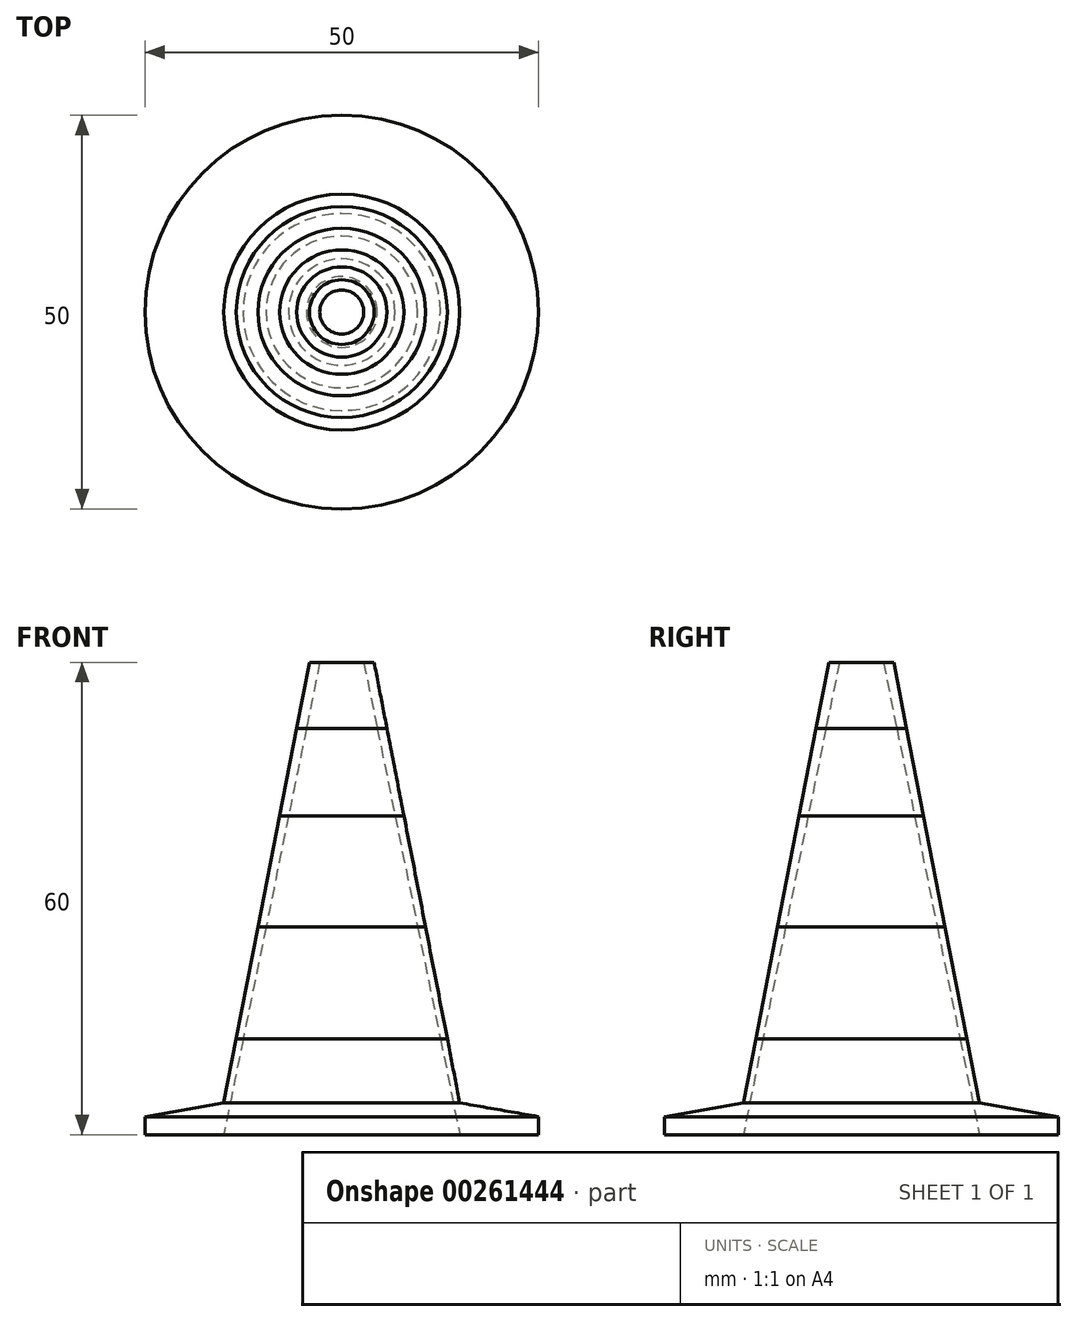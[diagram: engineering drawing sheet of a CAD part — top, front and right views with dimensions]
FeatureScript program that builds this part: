
annotation { "Feature Type Name" : "Feature", "Feature Type Description" : "" }
export const myFeature = defineFeature(function(context is Context, id is Id, definition is map)
    precondition{}
    {
        {
            var Q0;
            Q0=qCreatedBy(makeId("Front.planeOp"),FACE);
            var sketch = newSketch(context, id + "F0", { "sketchPlane" : qUnion([Q0])});
            skLineSegment(sketch, "E0", {"start": v(-25, 0) * mm, "end": v(-25, 2.28) * mm});
            skLineSegment(sketch, "E1", {"start": v(-25, 2.28) * mm, "end": v(-14.98, 4.05) * mm});
            skLineSegment(sketch, "E2", {"start": v(-14.98, 4.05) * mm, "end": v(-4.1, 60) * mm});
            skLineSegment(sketch, "E3", {"start": v(-4.1, 60) * mm, "end": v(0, 60) * mm});
            skLineSegment(sketch, "E4", {"start": v(0, 60) * mm, "end": v(0, 0) * mm});
            skLineSegment(sketch, "E5", {"start": v(0, 0) * mm, "end": v(-25, 0) * mm});
            skLineSegment(sketch, "E6", {"start": v(-13.4, 12.2) * mm, "end": v(0, 12.2) * mm});
            skLineSegment(sketch, "E7", {"start": v(-10.64, 26.4) * mm, "end": v(0, 26.4) * mm});
            skLineSegment(sketch, "E8", {"start": v(-5.74, 51.6) * mm, "end": v(0, 51.6) * mm});
            skLineSegment(sketch, "E9", {"start": v(-7.9, 40.5) * mm, "end": v(0, 40.5) * mm});
            skSolve(sketch);
        }
        {
            var Q0;
            {var subQ0=sQuery(id+"F0.wireOp",EDGE,"E3");Q0=makeQuery(id+"F0.imprint","IMPRINT",FACE,{"disambiguationData":[TD([[makeQuery(id+"F0.imprint","IMPRINT",EDGE,{"derivedFrom":subQ0}),-1.0]])]});}
            var Q1;
            Q1=sQuery(id+"F0.wireOp",EDGE,"E4");
            revolve(context, id + "F1", {"entities" : qUnion([Q0]), "axis" : qUnion([Q1]), "revolveType" : RevolveType.FULL});
        }
        {
            var Q0;
            {var subQ0=sQuery(id+"F0.wireOp",EDGE,"E8");Q0=makeQuery(id+"F0.imprint","IMPRINT",FACE,{"disambiguationData":[TD([[makeQuery(id+"F0.imprint","IMPRINT",EDGE,{"derivedFrom":subQ0}),-1.0]])]});}
            var Q1;
            Q1=sQuery(id+"F0.wireOp",EDGE,"E4");
            revolve(context, id + "F2", {"entities" : qUnion([Q0]), "axis" : qUnion([Q1]), "revolveType" : RevolveType.FULL});
        }
        {
            var Q0;
            {var subQ0=sQuery(id+"F0.wireOp",EDGE,"E7");Q0=makeQuery(id+"F0.imprint","IMPRINT",FACE,{"disambiguationData":[TD([[makeQuery(id+"F0.imprint","IMPRINT",EDGE,{"derivedFrom":subQ0}),1.0]])]});}
            var Q1;
            Q1=sQuery(id+"F0.wireOp",EDGE,"E4");
            revolve(context, id + "F3", {"entities" : qUnion([Q0]), "axis" : qUnion([Q1]), "revolveType" : RevolveType.FULL});
        }
        {
            var Q0;
            {var subQ0=sQuery(id+"F0.wireOp",EDGE,"E6");Q0=makeQuery(id+"F0.imprint","IMPRINT",FACE,{"disambiguationData":[TD([[makeQuery(id+"F0.imprint","IMPRINT",EDGE,{"derivedFrom":subQ0}),1.0]])]});}
            var Q1;
            Q1=sQuery(id+"F0.wireOp",EDGE,"E4");
            revolve(context, id + "F4", {"entities" : qUnion([Q0]), "axis" : qUnion([Q1]), "revolveType" : RevolveType.FULL});
        }
        {
            var Q0;
            Q0=makeQuery(id+"F0.imprint","IMPRINT",FACE,{"disambiguationData":[TD([[makeQuery(id+"F0.imprint","IMPRINT",EDGE,{"derivedFrom":sQuery(id+"F0.wireOp",EDGE,"E0")}),-1.0]])]});
            var Q1;
            Q1=sQuery(id+"F0.wireOp",EDGE,"E4");
            revolve(context, id + "F5", {"entities" : qUnion([Q0]), "axis" : qUnion([Q1]), "revolveType" : RevolveType.FULL});
        }
        {
            var Q0;
            Q0=makeQuery(id+"F5.opRevolve","SWEPT_FACE",FACE,{"disambiguationData":[OSD([sQuery(id+"F0.wireOp",EDGE,"E5")])]});
            var sketch = newSketch(context, id + "F6", { "sketchPlane" : qUnion([Q0])});
            skCircle(sketch, "E10", {"center": v(0, 0) * mm, "radius": 15 * mm});
            skSolve(sketch);
        }
        {
            var Q0;
            Q0=makeQuery(id+"F6.imprint","IMPRINT",FACE,{"disambiguationData":[TD([[makeQuery(id+"F6.imprint","IMPRINT",EDGE,{"derivedFrom":sQuery(id+"F6.wireOp",EDGE,"E10")}),1.0]])]});
            extrude(context, id + "F7", {"entities" : qUnion([Q0]), "operationType" : NewBodyOperationType.REMOVE, "endBound" : BoundingType.THROUGH_ALL, "oppositeDirection" : true, "depth" : 25 * mm, "hasDraft" : true, "draftAngle" : 11.5 * degree, "draftPullDirection" : true});
        }
    });
